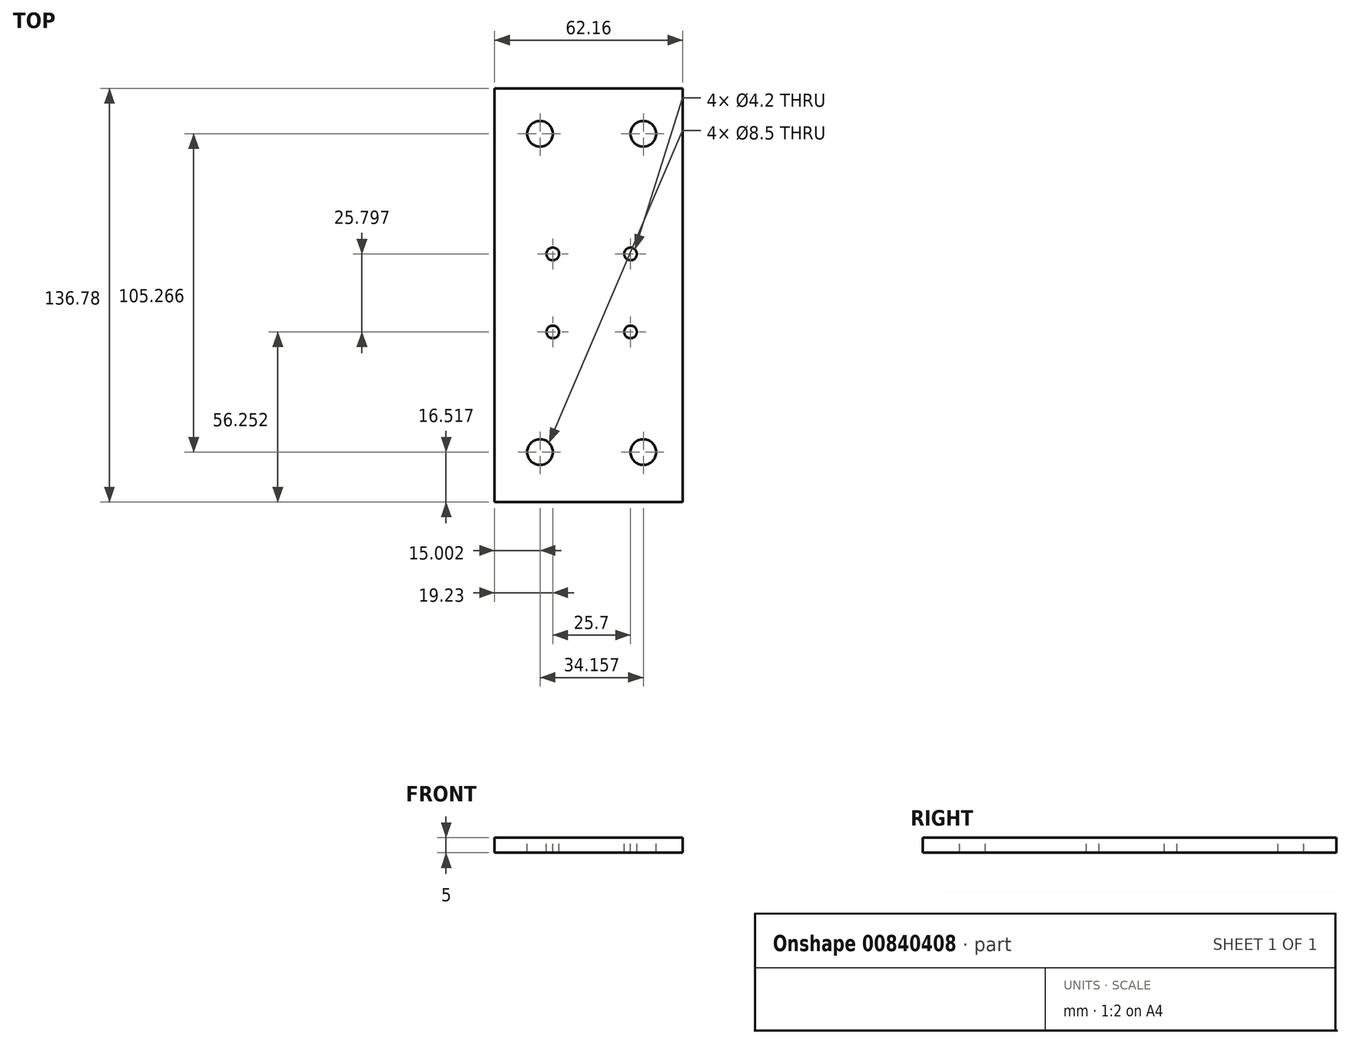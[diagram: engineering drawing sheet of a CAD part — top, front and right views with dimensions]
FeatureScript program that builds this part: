
annotation { "Feature Type Name" : "Feature", "Feature Type Description" : "" }
export const myFeature = defineFeature(function(context is Context, id is Id, definition is map)
    precondition{}
    {
        {
            var Q0;
            Q0=qCreatedBy(makeId("Top.planeOp"),FACE);
            var sketch = newSketch(context, id + "F0", { "sketchPlane" : qUnion([Q0])});
            skLineSegment(sketch, "E0.bottom", {"start": v(30.08, 67.63) * mm, "end": v(-32.08, 67.63) * mm});
            skLineSegment(sketch, "E0.top", {"start": v(30.08, -69.15) * mm, "end": v(-32.08, -69.15) * mm});
            skLineSegment(sketch, "E0.left", {"start": v(30.08, 67.63) * mm, "end": v(30.08, -69.15) * mm});
            skLineSegment(sketch, "E0.right", {"start": v(-32.08, 67.63) * mm, "end": v(-32.08, -69.15) * mm});
            skPoint(sketch, "E1", {"position": v(-12.6, 13.34) * mm});
            skPoint(sketch, "E2", {"position": v(13.1, 13.34) * mm});
            skPoint(sketch, "E3", {"position": v(-12.6, -12.45) * mm});
            skPoint(sketch, "E4", {"position": v(13.1, -12.45) * mm});
            skSolve(sketch);
        }
        {
            var Q0;
            Q0 = qSketchRegion(id + "F0", true);
            extrude(context, id + "F1", {"entities" : qUnion([Q0]), "endBound" : BoundingType.SYMMETRIC, "depth" : 5 * mm, "offsetDistance" : 25.4 * mm});
        }
        {
            var Q0;
            Q0=makeQuery(id+"F1.opExtrude","CAP_FACE",FACE,{"disambiguationData":[OSD([sQuery(id+"F0.wireOp",EDGE,"E0.bottom"),sQuery(id+"F0.wireOp",EDGE,"E0.top"),sQuery(id+"F0.wireOp",EDGE,"E0.left"),sQuery(id+"F0.wireOp",EDGE,"E0.right")])],"isStart":false});
            var sketch = newSketch(context, id + "F2", { "sketchPlane" : qUnion([Q0])});
            skPoint(sketch, "E5", {"position": v(-12.85, 12.9) * mm});
            skPoint(sketch, "E6", {"position": v(12.85, 12.9) * mm});
            skPoint(sketch, "E7", {"position": v(-12.85, -12.9) * mm});
            skPoint(sketch, "E8", {"position": v(12.85, -12.9) * mm});
            skSolve(sketch);
        }
        {
            var Q0;
            Q0=sQuery(id+"F2.wireOp",VERTEX,"E7");
            var Q1;
            Q1=sQuery(id+"F2.wireOp",VERTEX,"E5");
            var Q2;
            Q2=sQuery(id+"F2.wireOp",VERTEX,"E8");
            var Q3;
            Q3=sQuery(id+"F2.wireOp",VERTEX,"E6");
            var Q4;
            Q4=makeQuery(id+"F1.opExtrude","SWEPT_BODY",BODY,{"disambiguationData":[OSD([sQuery(id+"F0.wireOp",EDGE,"E0.bottom"),sQuery(id+"F0.wireOp",EDGE,"E0.top"),sQuery(id+"F0.wireOp",EDGE,"E0.left"),sQuery(id+"F0.wireOp",EDGE,"E0.right")])]});
            hole(context, id + "F3", {"style" : HoleStyle.SIMPLE, "endStyle" : HoleEndStyle.THROUGH, "standardTappedOrClearance" : lookupTablePath({ "standard" : "ISO", "engagement" : "75%", "pitch" : "0.8 mm", "size" : "M5", "type" : "Tapped" }), "standardBlindInLast" : lookupTablePath({ "standard" : "ISO", "engagement" : "75%", "pitch" : "0.8 mm", "size" : "M5", "type" : "Tapped" }), "holeDiameter" : 4.2 * mm, "majorDiameter" : 5 * mm, "showTappedDepth" : true, "tappedDepth" : 12.7 * mm, "tapClearance" : 3, "locations" : qUnion([Q0, Q1, Q2, Q3]), "scope" : qUnion([Q4])});
        }
        {
            var Q0;
            Q0=makeQuery(id+"F1.opExtrude","CAP_FACE",FACE,{"disambiguationData":[OSD([sQuery(id+"F0.wireOp",EDGE,"E0.bottom"),sQuery(id+"F0.wireOp",EDGE,"E0.top"),sQuery(id+"F0.wireOp",EDGE,"E0.left"),sQuery(id+"F0.wireOp",EDGE,"E0.right")])],"isStart":false});
            var sketch = newSketch(context, id + "F4", { "sketchPlane" : qUnion([Q0])});
            skPoint(sketch, "E9", {"position": v(-17.08, 52.63) * mm});
            skPoint(sketch, "E10.MirrorP", {"position": v(17.08, 52.63) * mm});
            skPoint(sketch, "E11.MirrorP", {"position": v(-17.08, -52.63) * mm});
            skPoint(sketch, "E12.MirrorP", {"position": v(17.08, -52.63) * mm});
            skSolve(sketch);
        }
        {
            var Q0;
            Q0=sQuery(id+"F4.wireOp",VERTEX,"E9");
            var Q1;
            Q1=sQuery(id+"F4.wireOp",VERTEX,"E10.MirrorP");
            var Q2;
            Q2=sQuery(id+"F4.wireOp",VERTEX,"E12.MirrorP");
            var Q3;
            Q3=sQuery(id+"F4.wireOp",VERTEX,"E11.MirrorP");
            var Q4;
            Q4=makeQuery(id+"F1.opExtrude","SWEPT_BODY",BODY,{"disambiguationData":[OSD([sQuery(id+"F0.wireOp",EDGE,"E0.bottom"),sQuery(id+"F0.wireOp",EDGE,"E0.top"),sQuery(id+"F0.wireOp",EDGE,"E0.left"),sQuery(id+"F0.wireOp",EDGE,"E0.right")])]});
            hole(context, id + "F5", {"style" : HoleStyle.SIMPLE, "endStyle" : HoleEndStyle.BLIND, "standardTappedOrClearance" : lookupTablePath({ "standard" : "ISO", "engagement" : "75%", "pitch" : "1.5 mm", "size" : "M10", "type" : "Tapped" }), "standardBlindInLast" : lookupTablePath({ "standard" : "ISO", "engagement" : "75%", "pitch" : "1.5 mm", "size" : "M10", "type" : "Tapped" }), "holeDiameter" : 8.5 * mm, "majorDiameter" : 10 * mm, "showTappedDepth" : true, "holeDepth" : 17.2 * mm, "tappedDepth" : 12.7 * mm, "tapClearance" : 3, "locations" : qUnion([Q0, Q1, Q2, Q3]), "scope" : qUnion([Q4])});
        }
    });
